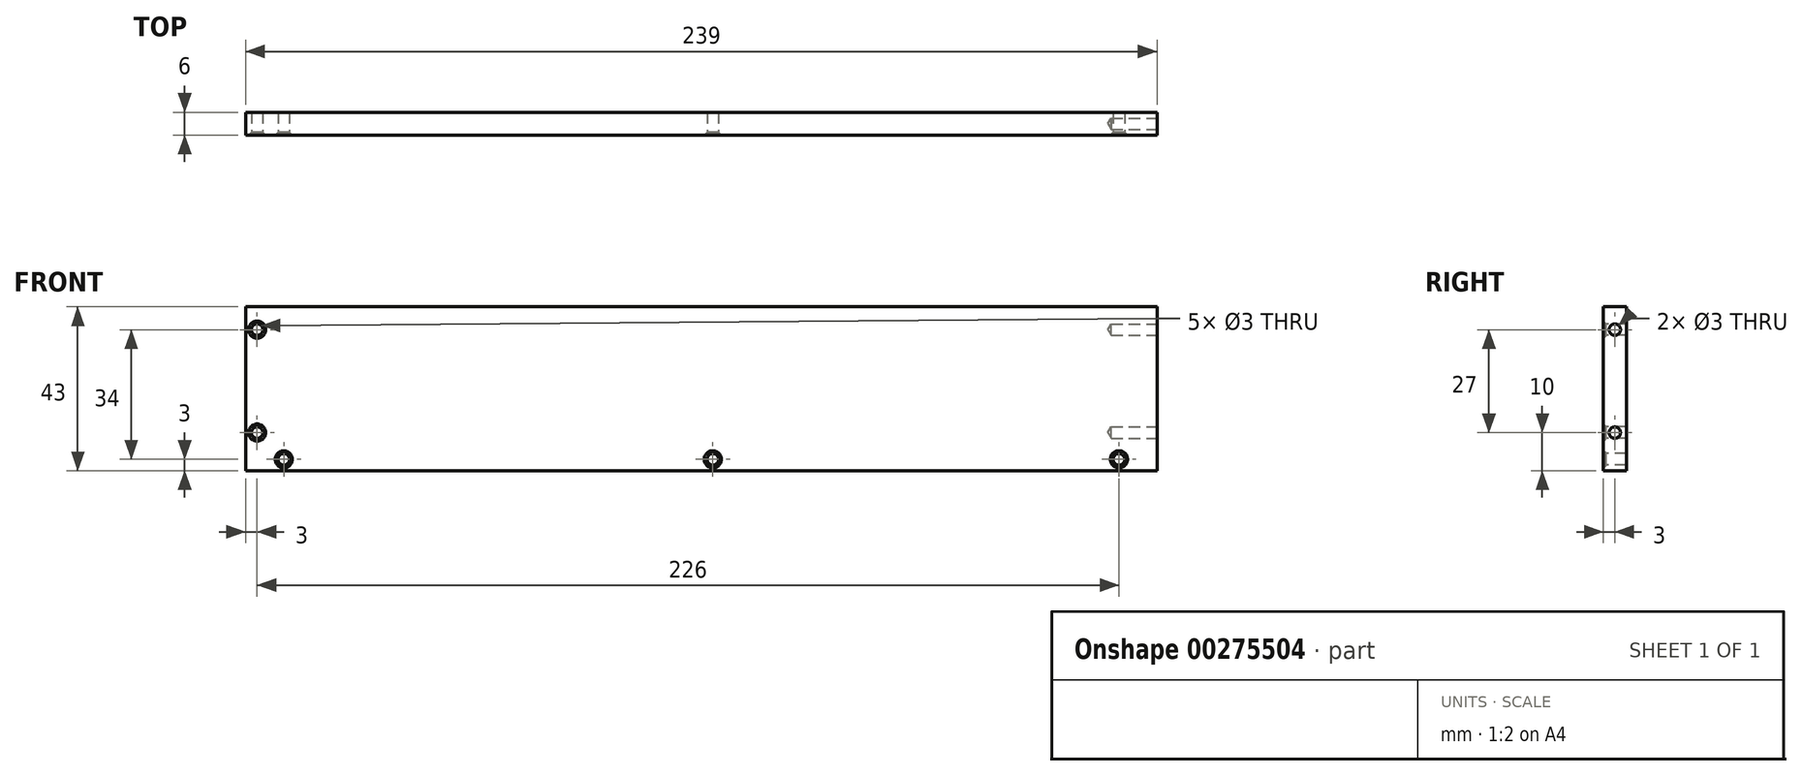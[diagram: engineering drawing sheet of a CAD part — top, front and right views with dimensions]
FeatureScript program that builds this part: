
annotation { "Feature Type Name" : "Feature", "Feature Type Description" : "" }
export const myFeature = defineFeature(function(context is Context, id is Id, definition is map)
    precondition{}
    {
        {
            var Q0;
            Q0=qCreatedBy(makeId("Top.planeOp"),FACE);
            var sketch = newSketch(context, id + "F0", { "sketchPlane" : qUnion([Q0])});
            skLineSegment(sketch, "E0.bottom", {"start": v(0, 0) * mm, "end": v(239, 0) * mm});
            skLineSegment(sketch, "E0.top", {"start": v(0, 6) * mm, "end": v(239, 6) * mm});
            skLineSegment(sketch, "E0.left", {"start": v(0, 0) * mm, "end": v(0, 6) * mm});
            skLineSegment(sketch, "E0.right", {"start": v(239, 0) * mm, "end": v(239, 6) * mm});
            skSolve(sketch);
        }
        {
            var Q0;
            Q0=makeQuery(id+"F0.imprint","IMPRINT",FACE,{"disambiguationData":[TD([[makeQuery(id+"F0.imprint","IMPRINT",EDGE,{"derivedFrom":sQuery(id+"F0.wireOp",EDGE,"E0.bottom")}),1.0]])]});
            extrude(context, id + "F1", {"entities" : qUnion([Q0]), "depth" : 43 * mm});
        }
        {
            var Q0;
            Q0=makeQuery(id+"F1.opExtrude","SWEPT_FACE",FACE,{"disambiguationData":[OSD([sQuery(id+"F0.wireOp",EDGE,"E0.right")])]});
            var sketch = newSketch(context, id + "F2", { "sketchPlane" : qUnion([Q0])});
            skPoint(sketch, "E1", {"position": v(3, 37) * mm});
            skPoint(sketch, "E1.positionSnap0", {"position": v(3, 43) * mm});
            skPoint(sketch, "E2", {"position": v(3, 10) * mm});
            skPoint(sketch, "E2.positionSnap0", {"position": v(3, 0) * mm});
            skSolve(sketch);
        }
        {
            var Q0;
            Q0=sQuery(id+"F2.wireOp",VERTEX,"E1");
            var Q1;
            Q1=sQuery(id+"F2.wireOp",VERTEX,"E2");
            var Q2;
            Q2=makeQuery(id+"F1.opExtrude","SWEPT_BODY",BODY,{"disambiguationData":[OSD([sQuery(id+"F0.wireOp",EDGE,"E0.bottom"),sQuery(id+"F0.wireOp",EDGE,"E0.top"),sQuery(id+"F0.wireOp",EDGE,"E0.left"),sQuery(id+"F0.wireOp",EDGE,"E0.right")])]});
            hole(context, id + "F3", {"style" : HoleStyle.SIMPLE, "endStyle" : HoleEndStyle.BLIND, "holeDiameter" : 3 * mm, "holeDepth" : 12 * mm, "tappedDepth" : 12 * mm, "tapClearance" : 3, "locations" : qUnion([Q0, Q1]), "scope" : qUnion([Q2])});
        }
        {
            var Q0;
            Q0=makeQuery(id+"F1.opExtrude","SWEPT_FACE",FACE,{"disambiguationData":[OSD([sQuery(id+"F0.wireOp",EDGE,"E0.bottom")])]});
            var sketch = newSketch(context, id + "F4", { "sketchPlane" : qUnion([Q0])});
            skPoint(sketch, "E3", {"position": v(3, 10) * mm});
            skPoint(sketch, "E4", {"position": v(3, 37) * mm});
            skSolve(sketch);
        }
        {
            var Q0;
            Q0=sQuery(id+"F4.wireOp",VERTEX,"E4");
            var Q1;
            Q1=sQuery(id+"F4.wireOp",VERTEX,"E3");
            var Q2;
            Q2=makeQuery(id+"F1.opExtrude","SWEPT_BODY",BODY,{"disambiguationData":[OSD([sQuery(id+"F0.wireOp",EDGE,"E0.bottom"),sQuery(id+"F0.wireOp",EDGE,"E0.top"),sQuery(id+"F0.wireOp",EDGE,"E0.left"),sQuery(id+"F0.wireOp",EDGE,"E0.right")])]});
            hole(context, id + "F5", {"style" : HoleStyle.C_SINK, "endStyle" : HoleEndStyle.BLIND, "holeDiameter" : 3 * mm, "cSinkDiameter" : 4.5 * mm, "cSinkAngle" : 90 * degree, "holeDepth" : 12 * mm, "tappedDepth" : 12 * mm, "tapClearance" : 3, "locations" : qUnion([Q0, Q1]), "scope" : qUnion([Q2])});
        }
        {
            var Q0;
            Q0=makeQuery(id+"F1.opExtrude","SWEPT_FACE",FACE,{"disambiguationData":[OSD([sQuery(id+"F0.wireOp",EDGE,"E0.bottom")])]});
            var sketch = newSketch(context, id + "F6", { "sketchPlane" : qUnion([Q0])});
            skPoint(sketch, "E5", {"position": v(10, 3) * mm});
            skPoint(sketch, "E6", {"position": v(122.5, 3) * mm});
            skPoint(sketch, "E7", {"position": v(229, 3) * mm});
            skSolve(sketch);
        }
        {
            var Q0;
            Q0=sQuery(id+"F6.wireOp",VERTEX,"E6");
            var Q1;
            Q1=sQuery(id+"F6.wireOp",VERTEX,"E7");
            var Q2;
            Q2=sQuery(id+"F6.wireOp",VERTEX,"E5");
            var Q3;
            Q3=makeQuery(id+"F1.opExtrude","SWEPT_BODY",BODY,{"disambiguationData":[OSD([sQuery(id+"F0.wireOp",EDGE,"E0.bottom"),sQuery(id+"F0.wireOp",EDGE,"E0.top"),sQuery(id+"F0.wireOp",EDGE,"E0.left"),sQuery(id+"F0.wireOp",EDGE,"E0.right")])]});
            hole(context, id + "F7", {"style" : HoleStyle.C_SINK, "endStyle" : HoleEndStyle.THROUGH, "holeDiameter" : 3 * mm, "cSinkDiameter" : 4.5 * mm, "cSinkAngle" : 90 * degree, "tappedDepth" : 12 * mm, "tapClearance" : 3, "locations" : qUnion([Q0, Q1, Q2]), "scope" : qUnion([Q3])});
        }
    });
